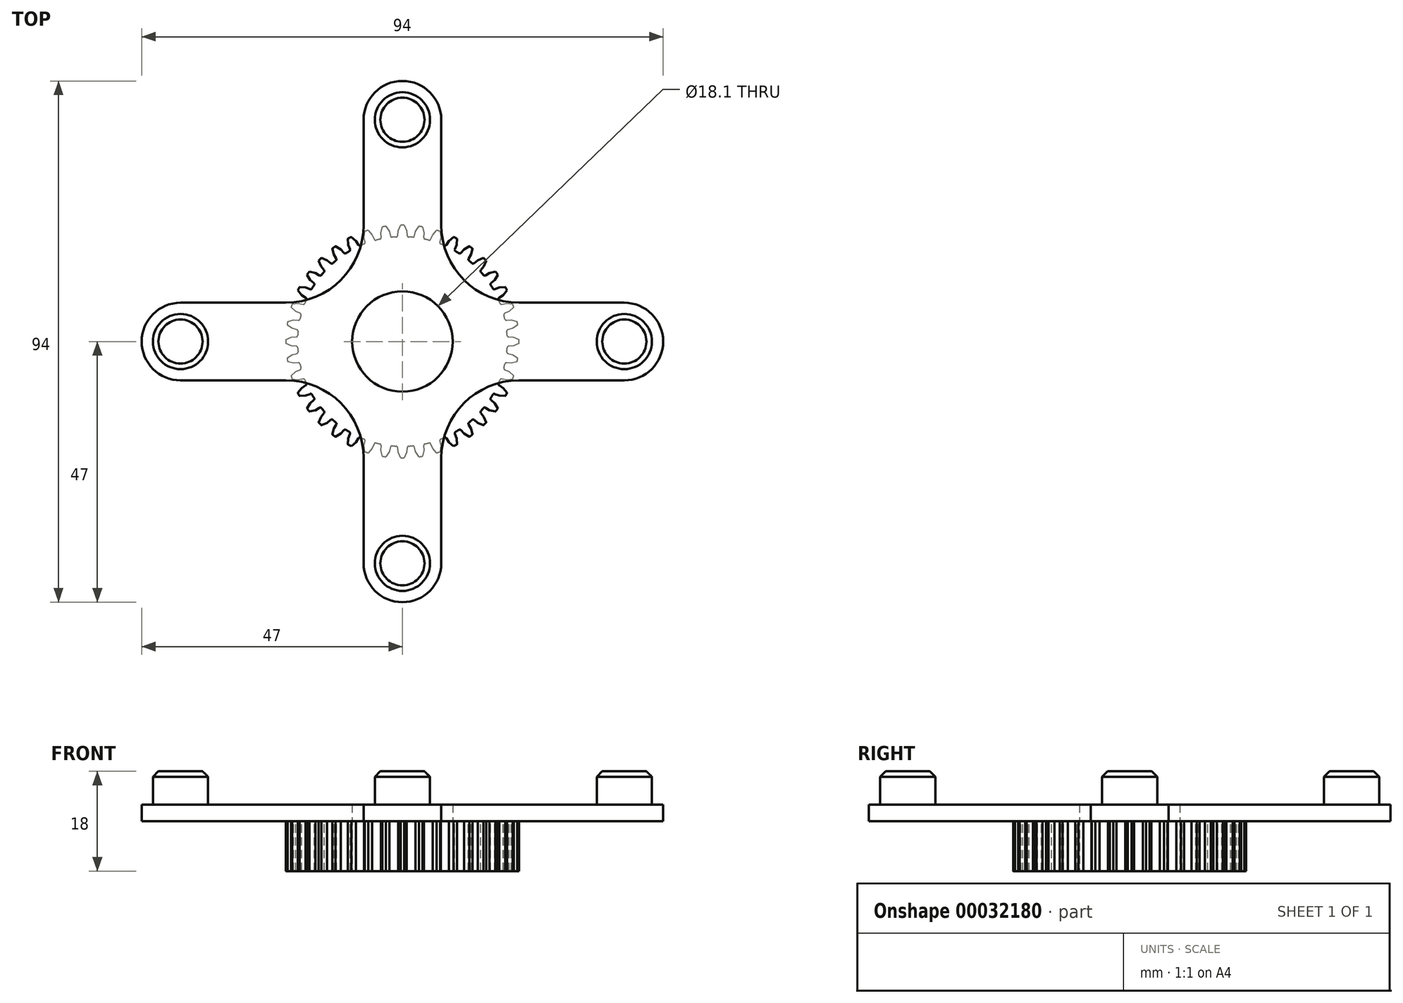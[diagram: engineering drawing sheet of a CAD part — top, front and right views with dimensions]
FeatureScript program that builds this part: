
annotation { "Feature Type Name" : "Feature", "Feature Type Description" : "" }
export const myFeature = defineFeature(function(context is Context, id is Id, definition is map)
    precondition{}
    {
        {
            var Q0;
            Q0=qCreatedBy(makeId("Top.planeOp"),FACE);
            var sketch = newSketch(context, id + "F0", { "sketchPlane" : qUnion([Q0])});
            skCircle(sketch, "E0", {"center": v(0, 0) * mm, "radius": 1 * mm});
            skCircle(sketch, "E1", {"center": v(0, 0) * mm, "radius": 52.75 * mm});
            skCircle(sketch, "E2", {"center": v(0, 40) * mm, "radius": 1 * mm});
            skCircle(sketch, "E3", {"center": v(40, 0) * mm, "radius": 1 * mm});
            skCircle(sketch, "E4", {"center": v(0, -40) * mm, "radius": 1 * mm});
            skCircle(sketch, "E5", {"center": v(-40, 0) * mm, "radius": 1 * mm});
            skCircle(sketch, "E6", {"center": v(0, 40) * mm, "radius": 4.97 * mm});
            skCircle(sketch, "E7", {"center": v(-40, 0) * mm, "radius": 4.97 * mm});
            skCircle(sketch, "E8", {"center": v(40, 0) * mm, "radius": 4.97 * mm});
            skCircle(sketch, "E9", {"center": v(0, -40) * mm, "radius": 4.97 * mm});
            skCircle(sketch, "E10", {"center": v(0, 0) * mm, "radius": 40 * mm, "construction": true});
            skArc(sketch, "E11.0.startCap", {"start": v(-7, 40) * mm, "mid": v(0, 47) * mm, "end": v(7, 40) * mm});
            skArc(sketch, "E11.0.endCap", {"start": v(7, -40) * mm, "mid": v(0, -47) * mm, "end": v(-7, -40) * mm});
            skLineSegment(sketch, "E11.0.left", {"start": v(7, 40) * mm, "end": v(7, 21) * mm});
            skLineSegment(sketch, "E11.0.right", {"start": v(-7, 40) * mm, "end": v(-7, 21) * mm});
            skArc(sketch, "E12.0.startCap", {"start": v(40, 7) * mm, "mid": v(47, 0) * mm, "end": v(40, -7) * mm});
            skArc(sketch, "E12.0.endCap", {"start": v(-40, -7) * mm, "mid": v(-47, 0) * mm, "end": v(-40, 7) * mm});
            skLineSegment(sketch, "E12.0.left", {"start": v(40, -7) * mm, "end": v(21, -7) * mm});
            skLineSegment(sketch, "E12.0.right", {"start": v(40, 7) * mm, "end": v(21, 7) * mm});
            skLineSegment(sketch, "E13.trimOffspring", {"start": v(-21, 7) * mm, "end": v(-40, 7) * mm});
            skLineSegment(sketch, "E14.trimOffspring", {"start": v(-7, -21) * mm, "end": v(-7, -40) * mm});
            skLineSegment(sketch, "E15.trimOffspring", {"start": v(7, -21) * mm, "end": v(7, -40) * mm});
            skLineSegment(sketch, "E16.trimOffspring", {"start": v(-21, -7) * mm, "end": v(-40, -7) * mm});
            skPoint(sketch, "E17.visualSharp", {"position": v(-7, 7) * mm});
            skArc(sketch, "E17.filletArc", {"start": v(-21, 7) * mm, "mid": v(-11.1, 11.1) * mm, "end": v(-7, 21) * mm});
            skPoint(sketch, "E18.visualSharp", {"position": v(-7, -7) * mm});
            skArc(sketch, "E18.filletArc", {"start": v(-7, -21) * mm, "mid": v(-11.1, -11.1) * mm, "end": v(-21, -7) * mm});
            skPoint(sketch, "E19.visualSharp", {"position": v(7, -7) * mm});
            skArc(sketch, "E19.filletArc", {"start": v(21, -7) * mm, "mid": v(11.1, -11.1) * mm, "end": v(7, -21) * mm});
            skPoint(sketch, "E20.visualSharp", {"position": v(7, 7) * mm});
            skArc(sketch, "E20.filletArc", {"start": v(7, 21) * mm, "mid": v(11.1, 11.1) * mm, "end": v(21, 7) * mm});
            skCircle(sketch, "E21", {"center": v(0, 0) * mm, "radius": 5 * mm});
            skCircle(sketch, "E22", {"center": v(0, 0) * mm, "radius": 14 * mm});
            skCircle(sketch, "E23", {"center": v(0, 0) * mm, "radius": 47 * mm, "construction": true});
            skSolve(sketch);
        }
        {
            var Q0;
            Q0=makeQuery(id+"F0.imprint","IMPRINT",FACE,{"disambiguationData":[TD([[makeQuery(id+"F0.imprint","IMPRINT",EDGE,{"derivedFrom":sQuery(id+"F0.wireOp",EDGE,"E6")}),-1.0]])]});
            var Q1;
            Q1=makeQuery(id+"F0.imprint","IMPRINT",FACE,{"disambiguationData":[TD([[makeQuery(id+"F0.imprint","IMPRINT",EDGE,{"derivedFrom":sQuery(id+"F0.wireOp",EDGE,"E5")}),1.0]])]});
            var Q2;
            Q2=makeQuery(id+"F0.imprint","IMPRINT",FACE,{"disambiguationData":[TD([[makeQuery(id+"F0.imprint","IMPRINT",EDGE,{"derivedFrom":sQuery(id+"F0.wireOp",EDGE,"E21")}),-1.0]])]});
            var Q3;
            Q3=makeQuery(id+"F0.imprint","IMPRINT",FACE,{"disambiguationData":[TD([[makeQuery(id+"F0.imprint","IMPRINT",EDGE,{"derivedFrom":sQuery(id+"F0.wireOp",EDGE,"E3")}),1.0]])]});
            var Q4;
            Q4=makeQuery(id+"F0.imprint","IMPRINT",FACE,{"disambiguationData":[TD([[makeQuery(id+"F0.imprint","IMPRINT",EDGE,{"derivedFrom":sQuery(id+"F0.wireOp",EDGE,"E2")}),1.0]])]});
            var Q5;
            Q5=makeQuery(id+"F0.imprint","IMPRINT",FACE,{"disambiguationData":[TD([[makeQuery(id+"F0.imprint","IMPRINT",EDGE,{"derivedFrom":sQuery(id+"F0.wireOp",EDGE,"E4")}),1.0]])]});
            var Q6;
            Q6=makeQuery(id+"F0.imprint","IMPRINT",FACE,{"disambiguationData":[TD([[makeQuery(id+"F0.imprint","IMPRINT",EDGE,{"derivedFrom":sQuery(id+"F0.wireOp",EDGE,"E5")}),-1.0]])]});
            var Q7;
            Q7=makeQuery(id+"F0.imprint","IMPRINT",FACE,{"disambiguationData":[TD([[makeQuery(id+"F0.imprint","IMPRINT",EDGE,{"derivedFrom":sQuery(id+"F0.wireOp",EDGE,"E4")}),-1.0]])]});
            var Q8;
            Q8=makeQuery(id+"F0.imprint","IMPRINT",FACE,{"disambiguationData":[TD([[makeQuery(id+"F0.imprint","IMPRINT",EDGE,{"derivedFrom":sQuery(id+"F0.wireOp",EDGE,"E3")}),-1.0]])]});
            var Q9;
            Q9=makeQuery(id+"F0.imprint","IMPRINT",FACE,{"disambiguationData":[TD([[makeQuery(id+"F0.imprint","IMPRINT",EDGE,{"derivedFrom":sQuery(id+"F0.wireOp",EDGE,"E2")}),-1.0]])]});
            extrude(context, id + "F1", {"entities" : qUnion([Q0, Q1, Q2, Q3, Q4, Q5, Q6, Q7, Q8, Q9]), "depth" : 3 * mm});
        }
        {
            var Q0;
            Q0=makeQuery(id+"F0.imprint","IMPRINT",FACE,{"disambiguationData":[TD([[makeQuery(id+"F0.imprint","IMPRINT",EDGE,{"derivedFrom":sQuery(id+"F0.wireOp",EDGE,"E5")}),1.0]])]});
            var Q1;
            Q1=makeQuery(id+"F0.imprint","IMPRINT",FACE,{"disambiguationData":[TD([[makeQuery(id+"F0.imprint","IMPRINT",EDGE,{"derivedFrom":sQuery(id+"F0.wireOp",EDGE,"E5")}),-1.0]])]});
            var Q2;
            Q2=makeQuery(id+"F0.imprint","IMPRINT",FACE,{"disambiguationData":[TD([[makeQuery(id+"F0.imprint","IMPRINT",EDGE,{"derivedFrom":sQuery(id+"F0.wireOp",EDGE,"E4")}),1.0]])]});
            var Q3;
            Q3=makeQuery(id+"F0.imprint","IMPRINT",FACE,{"disambiguationData":[TD([[makeQuery(id+"F0.imprint","IMPRINT",EDGE,{"derivedFrom":sQuery(id+"F0.wireOp",EDGE,"E4")}),-1.0]])]});
            var Q4;
            Q4=makeQuery(id+"F0.imprint","IMPRINT",FACE,{"disambiguationData":[TD([[makeQuery(id+"F0.imprint","IMPRINT",EDGE,{"derivedFrom":sQuery(id+"F0.wireOp",EDGE,"E3")}),-1.0]])]});
            var Q5;
            Q5=makeQuery(id+"F0.imprint","IMPRINT",FACE,{"disambiguationData":[TD([[makeQuery(id+"F0.imprint","IMPRINT",EDGE,{"derivedFrom":sQuery(id+"F0.wireOp",EDGE,"E3")}),1.0]])]});
            var Q6;
            Q6=makeQuery(id+"F0.imprint","IMPRINT",FACE,{"disambiguationData":[TD([[makeQuery(id+"F0.imprint","IMPRINT",EDGE,{"derivedFrom":sQuery(id+"F0.wireOp",EDGE,"E2")}),1.0]])]});
            var Q7;
            Q7=makeQuery(id+"F0.imprint","IMPRINT",FACE,{"disambiguationData":[TD([[makeQuery(id+"F0.imprint","IMPRINT",EDGE,{"derivedFrom":sQuery(id+"F0.wireOp",EDGE,"E2")}),-1.0]])]});
            extrude(context, id + "F2", {"entities" : qUnion([Q0, Q1, Q2, Q3, Q4, Q5, Q6, Q7]), "operationType" : NewBodyOperationType.ADD, "depth" : 9 * mm});
        }
        {
            var Q0;
            Q0=makeQuery(id+"F2.opExtrude","CAP_EDGE",EDGE,{"disambiguationData":[OSD([sQuery(id+"F0.wireOp",EDGE,"E7")])],"isStart":false});
            var Q1;
            Q1=makeQuery(id+"F2.opExtrude","CAP_EDGE",EDGE,{"disambiguationData":[OSD([sQuery(id+"F0.wireOp",EDGE,"E6")])],"isStart":false});
            var Q2;
            Q2=makeQuery(id+"F2.opExtrude","CAP_EDGE",EDGE,{"disambiguationData":[OSD([sQuery(id+"F0.wireOp",EDGE,"E8")])],"isStart":false});
            var Q3;
            Q3=makeQuery(id+"F2.opExtrude","CAP_EDGE",EDGE,{"disambiguationData":[OSD([sQuery(id+"F0.wireOp",EDGE,"E9")])],"isStart":false});
            var Q4;
            Q4=makeQuery(id+"FGKay2Df9lcGa7H_1.opExtrude","CAP_EDGE",EDGE,{"disambiguationData":[OSD([sQuery(id+"F0.wireOp",EDGE,"E21")])],"isStart":false});
            var Q5;
            Q5=makeQuery(id+"FGKay2Df9lcGa7H_1.opExtrude","CAP_EDGE",EDGE,{"disambiguationData":[OSD([sQuery(id+"F0.wireOp",EDGE,"E22")])],"isStart":false});
            chamfer(context, id + "F3", {"entities" : qUnion([Q0, Q1, Q2, Q3, Q4, Q5]), "width" : 1 * mm, "tangentPropagation" : true});
        }
        {
            var Q0;
            Q0=makeQuery(id+"F1.opExtrude","CAP_FACE",FACE,{"disambiguationData":[OSD([sQuery(id+"F0.wireOp",EDGE,"E11.0.startCap"),sQuery(id+"F0.wireOp",EDGE,"E11.0.endCap"),sQuery(id+"F0.wireOp",EDGE,"E11.0.left"),sQuery(id+"F0.wireOp",EDGE,"E11.0.right"),sQuery(id+"F0.wireOp",EDGE,"E12.0.startCap"),sQuery(id+"F0.wireOp",EDGE,"E12.0.endCap"),sQuery(id+"F0.wireOp",EDGE,"E12.0.left"),sQuery(id+"F0.wireOp",EDGE,"E12.0.right"),sQuery(id+"F0.wireOp",EDGE,"E13.trimOffspring"),sQuery(id+"F0.wireOp",EDGE,"E14.trimOffspring"),sQuery(id+"F0.wireOp",EDGE,"E15.trimOffspring"),sQuery(id+"F0.wireOp",EDGE,"E16.trimOffspring"),sQuery(id+"F0.wireOp",EDGE,"E17.filletArc"),sQuery(id+"F0.wireOp",EDGE,"E18.filletArc"),sQuery(id+"F0.wireOp",EDGE,"E19.filletArc"),sQuery(id+"F0.wireOp",EDGE,"E20.filletArc"),sQuery(id+"F0.wireOp",EDGE,"E21")])],"isStart":true});
            var sketch = newSketch(context, id + "F4", { "sketchPlane" : qUnion([Q0])});
            skArc(sketch, "E24", {"start": v(21, -0.33) * mm, "mid": v(21, -0.17) * mm, "end": v(21, 0) * mm});
            skArc(sketch, "E25", {"start": v(-12.5, 0) * mm, "mid": v(0, -12.5) * mm, "end": v(12.5, 0) * mm});
            skArc(sketch, "E26", {"start": v(0, -5) * mm, "mid": v(5, 0) * mm, "end": v(0, 5) * mm});
            skArc(sketch, "E27", {"start": v(-21, 0) * mm, "mid": v(-21, -0.17) * mm, "end": v(-21, -0.33) * mm});
            skArc(sketch, "E28", {"start": v(18.87, 1.14) * mm, "mid": v(18.84, 1.48) * mm, "end": v(18.81, 1.83) * mm});
            skArc(sketch, "E29", {"start": v(19.04, 2.15) * mm, "mid": v(18.86, 2.03) * mm, "end": v(18.81, 1.83) * mm});
            skLineSegment(sketch, "E30", {"start": v(19.04, 2.15) * mm, "end": v(19.86, 2.36) * mm});
            skArc(sketch, "E31", {"start": v(19.14, -0.86) * mm, "mid": v(18.95, -0.95) * mm, "end": v(18.87, -1.14) * mm});
            skLineSegment(sketch, "E32", {"start": v(19.86, 2.36) * mm, "end": v(20.8, 2.96) * mm});
            skArc(sketch, "E33", {"start": v(18.46, 4.07) * mm, "mid": v(18.38, 4.41) * mm, "end": v(18.3, 4.75) * mm});
            skLineSegment(sketch, "E34", {"start": v(19.14, -0.86) * mm, "end": v(19.98, -0.78) * mm});
            skArc(sketch, "E35", {"start": v(18.46, 5.1) * mm, "mid": v(18.31, 4.96) * mm, "end": v(18.3, 4.75) * mm});
            skLineSegment(sketch, "E36", {"start": v(19.98, -0.78) * mm, "end": v(21, -0.33) * mm});
            skLineSegment(sketch, "E37", {"start": v(18.46, 5.1) * mm, "end": v(19.25, 5.44) * mm});
            skArc(sketch, "E38", {"start": v(18.77, -3.84) * mm, "mid": v(18.57, -3.9) * mm, "end": v(18.46, -4.07) * mm});
            skLineSegment(sketch, "E39", {"start": v(19.25, 5.44) * mm, "end": v(20.07, 6.17) * mm});
            skArc(sketch, "E40", {"start": v(17.6, 6.91) * mm, "mid": v(17.46, 7.23) * mm, "end": v(17.33, 7.55) * mm});
            skLineSegment(sketch, "E41", {"start": v(18.77, -3.84) * mm, "end": v(19.62, -3.9) * mm});
            skArc(sketch, "E42", {"start": v(17.44, 7.93) * mm, "mid": v(17.31, 7.76) * mm, "end": v(17.33, 7.55) * mm});
            skLineSegment(sketch, "E43", {"start": v(19.62, -3.9) * mm, "end": v(20.69, -3.61) * mm});
            skLineSegment(sketch, "E44", {"start": v(17.44, 7.93) * mm, "end": v(18.16, 8.38) * mm});
            skArc(sketch, "E45", {"start": v(17.94, -6.73) * mm, "mid": v(17.73, -6.76) * mm, "end": v(17.6, -6.91) * mm});
            skLineSegment(sketch, "E46", {"start": v(18.16, 8.38) * mm, "end": v(18.86, 9.24) * mm});
            skArc(sketch, "E47", {"start": v(16.3, 9.58) * mm, "mid": v(16.11, 9.88) * mm, "end": v(15.93, 10.17) * mm});
            skLineSegment(sketch, "E48", {"start": v(17.94, -6.73) * mm, "end": v(18.77, -6.91) * mm});
            skArc(sketch, "E49", {"start": v(15.98, 10.56) * mm, "mid": v(15.89, 10.37) * mm, "end": v(15.93, 10.17) * mm});
            skLineSegment(sketch, "E50", {"start": v(18.77, -6.91) * mm, "end": v(19.87, -6.8) * mm});
            skLineSegment(sketch, "E51", {"start": v(15.98, 10.56) * mm, "end": v(16.62, 11.12) * mm});
            skArc(sketch, "E52", {"start": v(16.66, -9.45) * mm, "mid": v(16.45, -9.45) * mm, "end": v(16.3, -9.58) * mm});
            skLineSegment(sketch, "E53", {"start": v(16.62, 11.12) * mm, "end": v(17.18, 12.07) * mm});
            skArc(sketch, "E54", {"start": v(14.6, 12) * mm, "mid": v(14.37, 12.27) * mm, "end": v(14.14, 12.54) * mm});
            skLineSegment(sketch, "E55", {"start": v(16.66, -9.45) * mm, "end": v(17.45, -9.76) * mm});
            skArc(sketch, "E56", {"start": v(14.14, 12.93) * mm, "mid": v(14.07, 12.73) * mm, "end": v(14.14, 12.54) * mm});
            skLineSegment(sketch, "E57", {"start": v(17.45, -9.76) * mm, "end": v(18.56, -9.83) * mm});
            skLineSegment(sketch, "E58", {"start": v(14.14, 12.93) * mm, "end": v(14.68, 13.58) * mm});
            skArc(sketch, "E59", {"start": v(14.98, -11.94) * mm, "mid": v(14.77, -11.9) * mm, "end": v(14.6, -12) * mm});
            skLineSegment(sketch, "E60", {"start": v(14.68, 13.58) * mm, "end": v(15.08, 14.61) * mm});
            skArc(sketch, "E61", {"start": v(12.54, 14.14) * mm, "mid": v(12.27, 14.37) * mm, "end": v(12, 14.6) * mm});
            skLineSegment(sketch, "E62", {"start": v(14.98, -11.94) * mm, "end": v(15.71, -12.37) * mm});
            skArc(sketch, "E63", {"start": v(11.94, 14.98) * mm, "mid": v(11.9, 14.77) * mm, "end": v(12, 14.6) * mm});
            skLineSegment(sketch, "E64", {"start": v(15.71, -12.37) * mm, "end": v(16.8, -12.61) * mm});
            skArc(sketch, "E65", {"start": v(12.93, -14.14) * mm, "mid": v(12.73, -14.07) * mm, "end": v(12.54, -14.14) * mm});
            skLineSegment(sketch, "E66", {"start": v(11.94, 14.98) * mm, "end": v(12.37, 15.71) * mm});
            skLineSegment(sketch, "E67", {"start": v(12.93, -14.14) * mm, "end": v(13.58, -14.68) * mm});
            skLineSegment(sketch, "E68", {"start": v(12.37, 15.71) * mm, "end": v(12.61, 16.8) * mm});
            skArc(sketch, "E69", {"start": v(10.17, 15.93) * mm, "mid": v(9.88, 16.11) * mm, "end": v(9.58, 16.3) * mm});
            skLineSegment(sketch, "E70", {"start": v(13.58, -14.68) * mm, "end": v(14.61, -15.08) * mm});
            skArc(sketch, "E71", {"start": v(9.45, 16.66) * mm, "mid": v(9.45, 16.45) * mm, "end": v(9.58, 16.3) * mm});
            skArc(sketch, "E72", {"start": v(10.56, -15.98) * mm, "mid": v(10.37, -15.89) * mm, "end": v(10.17, -15.93) * mm});
            skLineSegment(sketch, "E73", {"start": v(9.45, 16.66) * mm, "end": v(9.76, 17.45) * mm});
            skLineSegment(sketch, "E74", {"start": v(10.56, -15.98) * mm, "end": v(11.12, -16.62) * mm});
            skLineSegment(sketch, "E75", {"start": v(9.76, 17.45) * mm, "end": v(9.83, 18.56) * mm});
            skArc(sketch, "E76", {"start": v(7.55, 17.33) * mm, "mid": v(7.23, 17.46) * mm, "end": v(6.91, 17.6) * mm});
            skLineSegment(sketch, "E77", {"start": v(11.12, -16.62) * mm, "end": v(12.07, -17.18) * mm});
            skArc(sketch, "E78", {"start": v(6.73, 17.94) * mm, "mid": v(6.76, 17.73) * mm, "end": v(6.91, 17.6) * mm});
            skArc(sketch, "E79", {"start": v(7.93, -17.44) * mm, "mid": v(7.76, -17.31) * mm, "end": v(7.55, -17.33) * mm});
            skLineSegment(sketch, "E80", {"start": v(6.73, 17.94) * mm, "end": v(6.91, 18.77) * mm});
            skLineSegment(sketch, "E81", {"start": v(7.93, -17.44) * mm, "end": v(8.38, -18.16) * mm});
            skLineSegment(sketch, "E82", {"start": v(6.91, 18.77) * mm, "end": v(6.8, 19.87) * mm});
            skArc(sketch, "E83", {"start": v(4.75, 18.3) * mm, "mid": v(4.41, 18.38) * mm, "end": v(4.07, 18.46) * mm});
            skLineSegment(sketch, "E84", {"start": v(8.38, -18.16) * mm, "end": v(9.24, -18.86) * mm});
            skArc(sketch, "E85", {"start": v(3.84, 18.77) * mm, "mid": v(3.9, 18.57) * mm, "end": v(4.07, 18.46) * mm});
            skArc(sketch, "E86", {"start": v(5.1, -18.46) * mm, "mid": v(4.96, -18.31) * mm, "end": v(4.75, -18.3) * mm});
            skLineSegment(sketch, "E87", {"start": v(3.84, 18.77) * mm, "end": v(3.9, 19.62) * mm});
            skLineSegment(sketch, "E88", {"start": v(5.1, -18.46) * mm, "end": v(5.44, -19.25) * mm});
            skLineSegment(sketch, "E89", {"start": v(3.9, 19.62) * mm, "end": v(3.61, 20.69) * mm});
            skArc(sketch, "E90", {"start": v(1.83, 18.81) * mm, "mid": v(1.48, 18.84) * mm, "end": v(1.14, 18.87) * mm});
            skLineSegment(sketch, "E91", {"start": v(5.44, -19.25) * mm, "end": v(6.17, -20.07) * mm});
            skArc(sketch, "E92", {"start": v(0.86, 19.14) * mm, "mid": v(0.95, 18.95) * mm, "end": v(1.14, 18.87) * mm});
            skArc(sketch, "E93", {"start": v(2.15, -19.04) * mm, "mid": v(2.03, -18.86) * mm, "end": v(1.83, -18.81) * mm});
            skLineSegment(sketch, "E94", {"start": v(0.86, 19.14) * mm, "end": v(0.78, 19.98) * mm});
            skArc(sketch, "E95", {"start": v(-1.14, 18.87) * mm, "mid": v(-1.48, 18.84) * mm, "end": v(-1.83, 18.81) * mm});
            skLineSegment(sketch, "E96", {"start": v(2.15, -19.04) * mm, "end": v(2.36, -19.86) * mm});
            skLineSegment(sketch, "E97", {"start": v(0.78, 19.98) * mm, "end": v(0.33, 21) * mm});
            skArc(sketch, "E98", {"start": v(-2.15, 19.04) * mm, "mid": v(-2.03, 18.86) * mm, "end": v(-1.83, 18.81) * mm});
            skLineSegment(sketch, "E99", {"start": v(2.36, -19.86) * mm, "end": v(2.96, -20.8) * mm});
            skArc(sketch, "E100", {"start": v(-0.86, -19.14) * mm, "mid": v(-0.95, -18.95) * mm, "end": v(-1.14, -18.87) * mm});
            skLineSegment(sketch, "E101", {"start": v(-2.15, 19.04) * mm, "end": v(-2.36, 19.86) * mm});
            skLineSegment(sketch, "E102", {"start": v(-0.86, -19.14) * mm, "end": v(-0.78, -19.98) * mm});
            skLineSegment(sketch, "E103", {"start": v(-2.36, 19.86) * mm, "end": v(-2.96, 20.8) * mm});
            skArc(sketch, "E104", {"start": v(-4.07, 18.46) * mm, "mid": v(-4.41, 18.38) * mm, "end": v(-4.75, 18.3) * mm});
            skLineSegment(sketch, "E105", {"start": v(-0.78, -19.98) * mm, "end": v(-0.33, -21) * mm});
            skArc(sketch, "E106", {"start": v(-5.1, 18.46) * mm, "mid": v(-4.96, 18.31) * mm, "end": v(-4.75, 18.3) * mm});
            skArc(sketch, "E107", {"start": v(-3.84, -18.77) * mm, "mid": v(-3.9, -18.57) * mm, "end": v(-4.07, -18.46) * mm});
            skLineSegment(sketch, "E108", {"start": v(-5.1, 18.46) * mm, "end": v(-5.44, 19.25) * mm});
            skLineSegment(sketch, "E109", {"start": v(-3.84, -18.77) * mm, "end": v(-3.9, -19.62) * mm});
            skLineSegment(sketch, "E110", {"start": v(-5.44, 19.25) * mm, "end": v(-6.17, 20.07) * mm});
            skArc(sketch, "E111", {"start": v(-6.91, 17.6) * mm, "mid": v(-7.23, 17.46) * mm, "end": v(-7.55, 17.33) * mm});
            skLineSegment(sketch, "E112", {"start": v(-3.9, -19.62) * mm, "end": v(-3.61, -20.69) * mm});
            skArc(sketch, "E113", {"start": v(-7.93, 17.44) * mm, "mid": v(-7.76, 17.31) * mm, "end": v(-7.55, 17.33) * mm});
            skArc(sketch, "E114", {"start": v(-6.73, -17.94) * mm, "mid": v(-6.76, -17.73) * mm, "end": v(-6.91, -17.6) * mm});
            skLineSegment(sketch, "E115", {"start": v(-7.93, 17.44) * mm, "end": v(-8.38, 18.16) * mm});
            skLineSegment(sketch, "E116", {"start": v(-6.73, -17.94) * mm, "end": v(-6.91, -18.77) * mm});
            skLineSegment(sketch, "E117", {"start": v(-8.38, 18.16) * mm, "end": v(-9.24, 18.86) * mm});
            skArc(sketch, "E118", {"start": v(-9.58, 16.3) * mm, "mid": v(-9.88, 16.11) * mm, "end": v(-10.17, 15.93) * mm});
            skLineSegment(sketch, "E119", {"start": v(-6.91, -18.77) * mm, "end": v(-6.8, -19.87) * mm});
            skArc(sketch, "E120", {"start": v(-10.56, 15.98) * mm, "mid": v(-10.37, 15.89) * mm, "end": v(-10.17, 15.93) * mm});
            skArc(sketch, "E121", {"start": v(-9.45, -16.66) * mm, "mid": v(-9.45, -16.45) * mm, "end": v(-9.58, -16.3) * mm});
            skLineSegment(sketch, "E122", {"start": v(-10.56, 15.98) * mm, "end": v(-11.12, 16.62) * mm});
            skLineSegment(sketch, "E123", {"start": v(-9.45, -16.66) * mm, "end": v(-9.76, -17.45) * mm});
            skLineSegment(sketch, "E124", {"start": v(-11.12, 16.62) * mm, "end": v(-12.07, 17.18) * mm});
            skArc(sketch, "E125", {"start": v(-12, 14.6) * mm, "mid": v(-12.27, 14.37) * mm, "end": v(-12.54, 14.14) * mm});
            skLineSegment(sketch, "E126", {"start": v(-9.76, -17.45) * mm, "end": v(-9.83, -18.56) * mm});
            skArc(sketch, "E127", {"start": v(-12.93, 14.14) * mm, "mid": v(-12.73, 14.07) * mm, "end": v(-12.54, 14.14) * mm});
            skArc(sketch, "E128", {"start": v(-11.94, -14.98) * mm, "mid": v(-11.9, -14.77) * mm, "end": v(-12, -14.6) * mm});
            skLineSegment(sketch, "E129", {"start": v(-12.93, 14.14) * mm, "end": v(-13.58, 14.68) * mm});
            skLineSegment(sketch, "E130", {"start": v(-11.94, -14.98) * mm, "end": v(-12.37, -15.71) * mm});
            skLineSegment(sketch, "E131", {"start": v(-13.58, 14.68) * mm, "end": v(-14.61, 15.08) * mm});
            skArc(sketch, "E132", {"start": v(-14.14, 12.54) * mm, "mid": v(-14.37, 12.27) * mm, "end": v(-14.6, 12) * mm});
            skLineSegment(sketch, "E133", {"start": v(-12.37, -15.71) * mm, "end": v(-12.61, -16.8) * mm});
            skArc(sketch, "E134", {"start": v(-14.98, 11.94) * mm, "mid": v(-14.77, 11.9) * mm, "end": v(-14.6, 12) * mm});
            skArc(sketch, "E135", {"start": v(-14.14, -12.93) * mm, "mid": v(-14.07, -12.73) * mm, "end": v(-14.14, -12.54) * mm});
            skLineSegment(sketch, "E136", {"start": v(-14.98, 11.94) * mm, "end": v(-15.71, 12.37) * mm});
            skLineSegment(sketch, "E137", {"start": v(-14.14, -12.93) * mm, "end": v(-14.68, -13.58) * mm});
            skLineSegment(sketch, "E138", {"start": v(-15.71, 12.37) * mm, "end": v(-16.8, 12.61) * mm});
            skArc(sketch, "E139", {"start": v(-15.93, 10.17) * mm, "mid": v(-16.11, 9.88) * mm, "end": v(-16.3, 9.58) * mm});
            skLineSegment(sketch, "E140", {"start": v(-14.68, -13.58) * mm, "end": v(-15.08, -14.61) * mm});
            skArc(sketch, "E141", {"start": v(-16.66, 9.45) * mm, "mid": v(-16.45, 9.45) * mm, "end": v(-16.3, 9.58) * mm});
            skArc(sketch, "E142", {"start": v(-15.98, -10.56) * mm, "mid": v(-15.89, -10.37) * mm, "end": v(-15.93, -10.17) * mm});
            skLineSegment(sketch, "E143", {"start": v(-16.66, 9.45) * mm, "end": v(-17.45, 9.76) * mm});
            skLineSegment(sketch, "E144", {"start": v(-15.98, -10.56) * mm, "end": v(-16.62, -11.12) * mm});
            skLineSegment(sketch, "E145", {"start": v(-17.45, 9.76) * mm, "end": v(-18.56, 9.83) * mm});
            skArc(sketch, "E146", {"start": v(-17.33, 7.55) * mm, "mid": v(-17.46, 7.23) * mm, "end": v(-17.6, 6.91) * mm});
            skLineSegment(sketch, "E147", {"start": v(-16.62, -11.12) * mm, "end": v(-17.18, -12.07) * mm});
            skArc(sketch, "E148", {"start": v(-17.94, 6.73) * mm, "mid": v(-17.73, 6.76) * mm, "end": v(-17.6, 6.91) * mm});
            skArc(sketch, "E149", {"start": v(-17.44, -7.93) * mm, "mid": v(-17.31, -7.76) * mm, "end": v(-17.33, -7.55) * mm});
            skLineSegment(sketch, "E150", {"start": v(-17.94, 6.73) * mm, "end": v(-18.77, 6.91) * mm});
            skLineSegment(sketch, "E151", {"start": v(-17.44, -7.93) * mm, "end": v(-18.16, -8.38) * mm});
            skLineSegment(sketch, "E152", {"start": v(-18.77, 6.91) * mm, "end": v(-19.87, 6.8) * mm});
            skArc(sketch, "E153", {"start": v(-18.3, 4.75) * mm, "mid": v(-18.38, 4.41) * mm, "end": v(-18.46, 4.07) * mm});
            skLineSegment(sketch, "E154", {"start": v(-18.16, -8.38) * mm, "end": v(-18.86, -9.24) * mm});
            skArc(sketch, "E155", {"start": v(-18.77, 3.84) * mm, "mid": v(-18.57, 3.9) * mm, "end": v(-18.46, 4.07) * mm});
            skArc(sketch, "E156", {"start": v(-18.46, -5.1) * mm, "mid": v(-18.31, -4.96) * mm, "end": v(-18.3, -4.75) * mm});
            skLineSegment(sketch, "E157", {"start": v(-18.77, 3.84) * mm, "end": v(-19.62, 3.9) * mm});
            skLineSegment(sketch, "E158", {"start": v(-18.46, -5.1) * mm, "end": v(-19.25, -5.44) * mm});
            skLineSegment(sketch, "E159", {"start": v(-19.62, 3.9) * mm, "end": v(-20.69, 3.61) * mm});
            skArc(sketch, "E160", {"start": v(-18.81, 1.83) * mm, "mid": v(-18.84, 1.48) * mm, "end": v(-18.87, 1.14) * mm});
            skLineSegment(sketch, "E161", {"start": v(-19.25, -5.44) * mm, "end": v(-20.07, -6.17) * mm});
            skArc(sketch, "E162", {"start": v(-19.14, 0.86) * mm, "mid": v(-18.95, 0.95) * mm, "end": v(-18.87, 1.14) * mm});
            skLineSegment(sketch, "E163", {"start": v(-19.14, 0.86) * mm, "end": v(-19.98, 0.78) * mm});
            skArc(sketch, "E164", {"start": v(-19.04, -2.15) * mm, "mid": v(-18.86, -2.03) * mm, "end": v(-18.81, -1.83) * mm});
            skLineSegment(sketch, "E165", {"start": v(-19.04, -2.15) * mm, "end": v(-19.86, -2.36) * mm});
            skLineSegment(sketch, "E166", {"start": v(-19.98, 0.78) * mm, "end": v(-21, 0.33) * mm});
            skLineSegment(sketch, "E167", {"start": v(-19.86, -2.36) * mm, "end": v(-20.8, -2.96) * mm});
            skLineSegment(sketch, "E168", {"start": v(-21, -0.33) * mm, "end": v(-19.98, -0.78) * mm});
            skLineSegment(sketch, "E169", {"start": v(-19.98, -0.78) * mm, "end": v(-19.14, -0.86) * mm});
            skArc(sketch, "E170", {"start": v(-18.87, -1.14) * mm, "mid": v(-18.95, -0.95) * mm, "end": v(-19.14, -0.86) * mm});
            skArc(sketch, "E171", {"start": v(-18.87, -1.14) * mm, "mid": v(-18.84, -1.48) * mm, "end": v(-18.81, -1.83) * mm});
            skLineSegment(sketch, "E172", {"start": v(-20.69, -3.61) * mm, "end": v(-19.62, -3.9) * mm});
            skLineSegment(sketch, "E173", {"start": v(-19.62, -3.9) * mm, "end": v(-18.77, -3.84) * mm});
            skArc(sketch, "E174", {"start": v(-18.46, -4.07) * mm, "mid": v(-18.57, -3.9) * mm, "end": v(-18.77, -3.84) * mm});
            skArc(sketch, "E175", {"start": v(-18.46, -4.07) * mm, "mid": v(-18.38, -4.41) * mm, "end": v(-18.3, -4.75) * mm});
            skLineSegment(sketch, "E176", {"start": v(-19.87, -6.8) * mm, "end": v(-18.77, -6.91) * mm});
            skLineSegment(sketch, "E177", {"start": v(-18.77, -6.91) * mm, "end": v(-17.94, -6.73) * mm});
            skArc(sketch, "E178", {"start": v(-17.6, -6.91) * mm, "mid": v(-17.73, -6.76) * mm, "end": v(-17.94, -6.73) * mm});
            skArc(sketch, "E179", {"start": v(-17.6, -6.91) * mm, "mid": v(-17.46, -7.23) * mm, "end": v(-17.33, -7.55) * mm});
            skLineSegment(sketch, "E180", {"start": v(-18.56, -9.83) * mm, "end": v(-17.45, -9.76) * mm});
            skLineSegment(sketch, "E181", {"start": v(-17.45, -9.76) * mm, "end": v(-16.66, -9.45) * mm});
            skArc(sketch, "E182", {"start": v(-16.3, -9.58) * mm, "mid": v(-16.45, -9.45) * mm, "end": v(-16.66, -9.45) * mm});
            skArc(sketch, "E183", {"start": v(-16.3, -9.58) * mm, "mid": v(-16.11, -9.88) * mm, "end": v(-15.93, -10.17) * mm});
            skLineSegment(sketch, "E184", {"start": v(-16.8, -12.61) * mm, "end": v(-15.71, -12.37) * mm});
            skLineSegment(sketch, "E185", {"start": v(-15.71, -12.37) * mm, "end": v(-14.98, -11.94) * mm});
            skArc(sketch, "E186", {"start": v(-14.6, -12) * mm, "mid": v(-14.77, -11.9) * mm, "end": v(-14.98, -11.94) * mm});
            skArc(sketch, "E187", {"start": v(-14.6, -12) * mm, "mid": v(-14.37, -12.27) * mm, "end": v(-14.14, -12.54) * mm});
            skLineSegment(sketch, "E188", {"start": v(-14.61, -15.08) * mm, "end": v(-13.58, -14.68) * mm});
            skLineSegment(sketch, "E189", {"start": v(-13.58, -14.68) * mm, "end": v(-12.93, -14.14) * mm});
            skArc(sketch, "E190", {"start": v(-12.54, -14.14) * mm, "mid": v(-12.73, -14.07) * mm, "end": v(-12.93, -14.14) * mm});
            skArc(sketch, "E191", {"start": v(-12.54, -14.14) * mm, "mid": v(-12.27, -14.37) * mm, "end": v(-12, -14.6) * mm});
            skLineSegment(sketch, "E192", {"start": v(-12.07, -17.18) * mm, "end": v(-11.12, -16.62) * mm});
            skLineSegment(sketch, "E193", {"start": v(-11.12, -16.62) * mm, "end": v(-10.56, -15.98) * mm});
            skArc(sketch, "E194", {"start": v(-10.17, -15.93) * mm, "mid": v(-10.37, -15.89) * mm, "end": v(-10.56, -15.98) * mm});
            skArc(sketch, "E195", {"start": v(-10.17, -15.93) * mm, "mid": v(-9.88, -16.11) * mm, "end": v(-9.58, -16.3) * mm});
            skLineSegment(sketch, "E196", {"start": v(-9.24, -18.86) * mm, "end": v(-8.38, -18.16) * mm});
            skLineSegment(sketch, "E197", {"start": v(-8.38, -18.16) * mm, "end": v(-7.93, -17.44) * mm});
            skArc(sketch, "E198", {"start": v(-7.55, -17.33) * mm, "mid": v(-7.76, -17.31) * mm, "end": v(-7.93, -17.44) * mm});
            skArc(sketch, "E199", {"start": v(-7.55, -17.33) * mm, "mid": v(-7.23, -17.46) * mm, "end": v(-6.91, -17.6) * mm});
            skLineSegment(sketch, "E200", {"start": v(-6.17, -20.07) * mm, "end": v(-5.44, -19.25) * mm});
            skLineSegment(sketch, "E201", {"start": v(-5.44, -19.25) * mm, "end": v(-5.1, -18.46) * mm});
            skArc(sketch, "E202", {"start": v(-4.75, -18.3) * mm, "mid": v(-4.96, -18.31) * mm, "end": v(-5.1, -18.46) * mm});
            skArc(sketch, "E203", {"start": v(-4.75, -18.3) * mm, "mid": v(-4.41, -18.38) * mm, "end": v(-4.07, -18.46) * mm});
            skLineSegment(sketch, "E204", {"start": v(-2.96, -20.8) * mm, "end": v(-2.36, -19.86) * mm});
            skLineSegment(sketch, "E205", {"start": v(-2.36, -19.86) * mm, "end": v(-2.15, -19.04) * mm});
            skArc(sketch, "E206", {"start": v(-1.83, -18.81) * mm, "mid": v(-2.03, -18.86) * mm, "end": v(-2.15, -19.04) * mm});
            skArc(sketch, "E207", {"start": v(-1.83, -18.81) * mm, "mid": v(-1.48, -18.84) * mm, "end": v(-1.14, -18.87) * mm});
            skLineSegment(sketch, "E208", {"start": v(0.33, -21) * mm, "end": v(0.78, -19.98) * mm});
            skLineSegment(sketch, "E209", {"start": v(0.78, -19.98) * mm, "end": v(0.86, -19.14) * mm});
            skArc(sketch, "E210", {"start": v(1.14, -18.87) * mm, "mid": v(0.95, -18.95) * mm, "end": v(0.86, -19.14) * mm});
            skArc(sketch, "E211", {"start": v(1.14, -18.87) * mm, "mid": v(1.48, -18.84) * mm, "end": v(1.83, -18.81) * mm});
            skLineSegment(sketch, "E212", {"start": v(3.61, -20.69) * mm, "end": v(3.9, -19.62) * mm});
            skLineSegment(sketch, "E213", {"start": v(3.9, -19.62) * mm, "end": v(3.84, -18.77) * mm});
            skArc(sketch, "E214", {"start": v(4.07, -18.46) * mm, "mid": v(3.9, -18.57) * mm, "end": v(3.84, -18.77) * mm});
            skArc(sketch, "E215", {"start": v(4.07, -18.46) * mm, "mid": v(4.41, -18.38) * mm, "end": v(4.75, -18.3) * mm});
            skLineSegment(sketch, "E216", {"start": v(6.8, -19.87) * mm, "end": v(6.91, -18.77) * mm});
            skLineSegment(sketch, "E217", {"start": v(6.91, -18.77) * mm, "end": v(6.73, -17.94) * mm});
            skArc(sketch, "E218", {"start": v(6.91, -17.6) * mm, "mid": v(6.76, -17.73) * mm, "end": v(6.73, -17.94) * mm});
            skArc(sketch, "E219", {"start": v(6.91, -17.6) * mm, "mid": v(7.23, -17.46) * mm, "end": v(7.55, -17.33) * mm});
            skLineSegment(sketch, "E220", {"start": v(9.83, -18.56) * mm, "end": v(9.76, -17.45) * mm});
            skLineSegment(sketch, "E221", {"start": v(9.76, -17.45) * mm, "end": v(9.45, -16.66) * mm});
            skArc(sketch, "E222", {"start": v(9.58, -16.3) * mm, "mid": v(9.45, -16.45) * mm, "end": v(9.45, -16.66) * mm});
            skArc(sketch, "E223", {"start": v(9.58, -16.3) * mm, "mid": v(9.88, -16.11) * mm, "end": v(10.17, -15.93) * mm});
            skLineSegment(sketch, "E224", {"start": v(12.61, -16.8) * mm, "end": v(12.37, -15.71) * mm});
            skLineSegment(sketch, "E225", {"start": v(12.37, -15.71) * mm, "end": v(11.94, -14.98) * mm});
            skArc(sketch, "E226", {"start": v(12, -14.6) * mm, "mid": v(11.9, -14.77) * mm, "end": v(11.94, -14.98) * mm});
            skArc(sketch, "E227", {"start": v(12, -14.6) * mm, "mid": v(12.27, -14.37) * mm, "end": v(12.54, -14.14) * mm});
            skLineSegment(sketch, "E228", {"start": v(15.08, -14.61) * mm, "end": v(14.68, -13.58) * mm});
            skLineSegment(sketch, "E229", {"start": v(14.68, -13.58) * mm, "end": v(14.14, -12.93) * mm});
            skArc(sketch, "E230", {"start": v(14.14, -12.54) * mm, "mid": v(14.07, -12.73) * mm, "end": v(14.14, -12.93) * mm});
            skArc(sketch, "E231", {"start": v(14.14, -12.54) * mm, "mid": v(14.37, -12.27) * mm, "end": v(14.6, -12) * mm});
            skLineSegment(sketch, "E232", {"start": v(17.18, -12.07) * mm, "end": v(16.62, -11.12) * mm});
            skLineSegment(sketch, "E233", {"start": v(16.62, -11.12) * mm, "end": v(15.98, -10.56) * mm});
            skArc(sketch, "E234", {"start": v(15.93, -10.17) * mm, "mid": v(15.89, -10.37) * mm, "end": v(15.98, -10.56) * mm});
            skArc(sketch, "E235", {"start": v(15.93, -10.17) * mm, "mid": v(16.11, -9.88) * mm, "end": v(16.3, -9.58) * mm});
            skLineSegment(sketch, "E236", {"start": v(18.86, -9.24) * mm, "end": v(18.16, -8.38) * mm});
            skLineSegment(sketch, "E237", {"start": v(18.16, -8.38) * mm, "end": v(17.44, -7.93) * mm});
            skArc(sketch, "E238", {"start": v(17.33, -7.55) * mm, "mid": v(17.31, -7.76) * mm, "end": v(17.44, -7.93) * mm});
            skArc(sketch, "E239", {"start": v(17.33, -7.55) * mm, "mid": v(17.46, -7.23) * mm, "end": v(17.6, -6.91) * mm});
            skLineSegment(sketch, "E240", {"start": v(20.07, -6.17) * mm, "end": v(19.25, -5.44) * mm});
            skLineSegment(sketch, "E241", {"start": v(19.25, -5.44) * mm, "end": v(18.46, -5.1) * mm});
            skArc(sketch, "E242", {"start": v(18.3, -4.75) * mm, "mid": v(18.31, -4.96) * mm, "end": v(18.46, -5.1) * mm});
            skArc(sketch, "E243", {"start": v(18.3, -4.75) * mm, "mid": v(18.38, -4.41) * mm, "end": v(18.46, -4.07) * mm});
            skLineSegment(sketch, "E244", {"start": v(20.8, -2.96) * mm, "end": v(19.86, -2.36) * mm});
            skLineSegment(sketch, "E245", {"start": v(19.86, -2.36) * mm, "end": v(19.04, -2.15) * mm});
            skArc(sketch, "E246", {"start": v(18.81, -1.83) * mm, "mid": v(18.86, -2.03) * mm, "end": v(19.04, -2.15) * mm});
            skArc(sketch, "E247", {"start": v(18.81, -1.83) * mm, "mid": v(18.84, -1.48) * mm, "end": v(18.87, -1.14) * mm});
            skLineSegment(sketch, "E248", {"start": v(21, 0.33) * mm, "end": v(19.98, 0.78) * mm});
            skLineSegment(sketch, "E249", {"start": v(19.98, 0.78) * mm, "end": v(19.14, 0.86) * mm});
            skArc(sketch, "E250", {"start": v(18.87, 1.14) * mm, "mid": v(18.95, 0.95) * mm, "end": v(19.14, 0.86) * mm});
            skLineSegment(sketch, "E251", {"start": v(20.69, 3.61) * mm, "end": v(19.62, 3.9) * mm});
            skLineSegment(sketch, "E252", {"start": v(19.62, 3.9) * mm, "end": v(18.77, 3.84) * mm});
            skArc(sketch, "E253", {"start": v(18.46, 4.07) * mm, "mid": v(18.57, 3.9) * mm, "end": v(18.77, 3.84) * mm});
            skLineSegment(sketch, "E254", {"start": v(19.87, 6.8) * mm, "end": v(18.77, 6.91) * mm});
            skLineSegment(sketch, "E255", {"start": v(18.77, 6.91) * mm, "end": v(17.94, 6.73) * mm});
            skArc(sketch, "E256", {"start": v(17.6, 6.91) * mm, "mid": v(17.73, 6.76) * mm, "end": v(17.94, 6.73) * mm});
            skLineSegment(sketch, "E257", {"start": v(18.56, 9.83) * mm, "end": v(17.45, 9.76) * mm});
            skLineSegment(sketch, "E258", {"start": v(17.45, 9.76) * mm, "end": v(16.66, 9.45) * mm});
            skArc(sketch, "E259", {"start": v(16.3, 9.58) * mm, "mid": v(16.45, 9.45) * mm, "end": v(16.66, 9.45) * mm});
            skLineSegment(sketch, "E260", {"start": v(16.8, 12.61) * mm, "end": v(15.71, 12.37) * mm});
            skLineSegment(sketch, "E261", {"start": v(15.71, 12.37) * mm, "end": v(14.98, 11.94) * mm});
            skArc(sketch, "E262", {"start": v(14.6, 12) * mm, "mid": v(14.77, 11.9) * mm, "end": v(14.98, 11.94) * mm});
            skLineSegment(sketch, "E263", {"start": v(14.61, 15.08) * mm, "end": v(13.58, 14.68) * mm});
            skLineSegment(sketch, "E264", {"start": v(13.58, 14.68) * mm, "end": v(12.93, 14.14) * mm});
            skArc(sketch, "E265", {"start": v(12.54, 14.14) * mm, "mid": v(12.73, 14.07) * mm, "end": v(12.93, 14.14) * mm});
            skLineSegment(sketch, "E266", {"start": v(12.07, 17.18) * mm, "end": v(11.12, 16.62) * mm});
            skLineSegment(sketch, "E267", {"start": v(11.12, 16.62) * mm, "end": v(10.56, 15.98) * mm});
            skArc(sketch, "E268", {"start": v(10.17, 15.93) * mm, "mid": v(10.37, 15.89) * mm, "end": v(10.56, 15.98) * mm});
            skLineSegment(sketch, "E269", {"start": v(9.24, 18.86) * mm, "end": v(8.38, 18.16) * mm});
            skLineSegment(sketch, "E270", {"start": v(8.38, 18.16) * mm, "end": v(7.93, 17.44) * mm});
            skArc(sketch, "E271", {"start": v(7.55, 17.33) * mm, "mid": v(7.76, 17.31) * mm, "end": v(7.93, 17.44) * mm});
            skLineSegment(sketch, "E272", {"start": v(6.17, 20.07) * mm, "end": v(5.44, 19.25) * mm});
            skLineSegment(sketch, "E273", {"start": v(5.44, 19.25) * mm, "end": v(5.1, 18.46) * mm});
            skArc(sketch, "E274", {"start": v(4.75, 18.3) * mm, "mid": v(4.96, 18.31) * mm, "end": v(5.1, 18.46) * mm});
            skLineSegment(sketch, "E275", {"start": v(2.96, 20.8) * mm, "end": v(2.36, 19.86) * mm});
            skLineSegment(sketch, "E276", {"start": v(2.36, 19.86) * mm, "end": v(2.15, 19.04) * mm});
            skArc(sketch, "E277", {"start": v(1.83, 18.81) * mm, "mid": v(2.03, 18.86) * mm, "end": v(2.15, 19.04) * mm});
            skLineSegment(sketch, "E278", {"start": v(-0.33, 21) * mm, "end": v(-0.78, 19.98) * mm});
            skLineSegment(sketch, "E279", {"start": v(-0.78, 19.98) * mm, "end": v(-0.86, 19.14) * mm});
            skArc(sketch, "E280", {"start": v(-1.14, 18.87) * mm, "mid": v(-0.95, 18.95) * mm, "end": v(-0.86, 19.14) * mm});
            skLineSegment(sketch, "E281", {"start": v(-3.61, 20.69) * mm, "end": v(-3.9, 19.62) * mm});
            skLineSegment(sketch, "E282", {"start": v(-3.9, 19.62) * mm, "end": v(-3.84, 18.77) * mm});
            skArc(sketch, "E283", {"start": v(-4.07, 18.46) * mm, "mid": v(-3.9, 18.57) * mm, "end": v(-3.84, 18.77) * mm});
            skLineSegment(sketch, "E284", {"start": v(-6.8, 19.87) * mm, "end": v(-6.91, 18.77) * mm});
            skLineSegment(sketch, "E285", {"start": v(-6.91, 18.77) * mm, "end": v(-6.73, 17.94) * mm});
            skArc(sketch, "E286", {"start": v(-6.91, 17.6) * mm, "mid": v(-6.76, 17.73) * mm, "end": v(-6.73, 17.94) * mm});
            skLineSegment(sketch, "E287", {"start": v(-9.83, 18.56) * mm, "end": v(-9.76, 17.45) * mm});
            skLineSegment(sketch, "E288", {"start": v(-9.76, 17.45) * mm, "end": v(-9.45, 16.66) * mm});
            skArc(sketch, "E289", {"start": v(-9.58, 16.3) * mm, "mid": v(-9.45, 16.45) * mm, "end": v(-9.45, 16.66) * mm});
            skLineSegment(sketch, "E290", {"start": v(-12.61, 16.8) * mm, "end": v(-12.37, 15.71) * mm});
            skLineSegment(sketch, "E291", {"start": v(-12.37, 15.71) * mm, "end": v(-11.94, 14.98) * mm});
            skArc(sketch, "E292", {"start": v(-12, 14.6) * mm, "mid": v(-11.9, 14.77) * mm, "end": v(-11.94, 14.98) * mm});
            skLineSegment(sketch, "E293", {"start": v(-15.08, 14.61) * mm, "end": v(-14.68, 13.58) * mm});
            skLineSegment(sketch, "E294", {"start": v(-14.68, 13.58) * mm, "end": v(-14.14, 12.93) * mm});
            skArc(sketch, "E295", {"start": v(-14.14, 12.54) * mm, "mid": v(-14.07, 12.73) * mm, "end": v(-14.14, 12.93) * mm});
            skLineSegment(sketch, "E296", {"start": v(-17.18, 12.07) * mm, "end": v(-16.62, 11.12) * mm});
            skLineSegment(sketch, "E297", {"start": v(-16.62, 11.12) * mm, "end": v(-15.98, 10.56) * mm});
            skArc(sketch, "E298", {"start": v(-15.93, 10.17) * mm, "mid": v(-15.89, 10.37) * mm, "end": v(-15.98, 10.56) * mm});
            skLineSegment(sketch, "E299", {"start": v(-18.86, 9.24) * mm, "end": v(-18.16, 8.38) * mm});
            skLineSegment(sketch, "E300", {"start": v(-18.16, 8.38) * mm, "end": v(-17.44, 7.93) * mm});
            skArc(sketch, "E301", {"start": v(-17.33, 7.55) * mm, "mid": v(-17.31, 7.76) * mm, "end": v(-17.44, 7.93) * mm});
            skLineSegment(sketch, "E302", {"start": v(-20.07, 6.17) * mm, "end": v(-19.25, 5.44) * mm});
            skLineSegment(sketch, "E303", {"start": v(-19.25, 5.44) * mm, "end": v(-18.46, 5.1) * mm});
            skArc(sketch, "E304", {"start": v(-18.3, 4.75) * mm, "mid": v(-18.31, 4.96) * mm, "end": v(-18.46, 5.1) * mm});
            skLineSegment(sketch, "E305", {"start": v(-20.8, 2.96) * mm, "end": v(-19.86, 2.36) * mm});
            skLineSegment(sketch, "E306", {"start": v(-19.86, 2.36) * mm, "end": v(-19.04, 2.15) * mm});
            skArc(sketch, "E307", {"start": v(-18.81, 1.83) * mm, "mid": v(-18.86, 2.03) * mm, "end": v(-19.04, 2.15) * mm});
            skArc(sketch, "E308", {"start": v(21, 0) * mm, "mid": v(21, 0.17) * mm, "end": v(21, 0.33) * mm});
            skArc(sketch, "E309", {"start": v(20.8, 2.96) * mm, "mid": v(20.74, 3.29) * mm, "end": v(20.69, 3.61) * mm});
            skArc(sketch, "E310", {"start": v(20.07, 6.17) * mm, "mid": v(19.97, 6.49) * mm, "end": v(19.87, 6.8) * mm});
            skArc(sketch, "E311", {"start": v(18.86, 9.24) * mm, "mid": v(18.71, 9.53) * mm, "end": v(18.56, 9.83) * mm});
            skArc(sketch, "E312", {"start": v(17.18, 12.07) * mm, "mid": v(16.99, 12.34) * mm, "end": v(16.8, 12.61) * mm});
            skArc(sketch, "E313", {"start": v(15.08, 14.61) * mm, "mid": v(14.85, 14.85) * mm, "end": v(14.61, 15.08) * mm});
            skArc(sketch, "E314", {"start": v(12.61, 16.8) * mm, "mid": v(12.34, 16.99) * mm, "end": v(12.07, 17.18) * mm});
            skArc(sketch, "E315", {"start": v(9.83, 18.56) * mm, "mid": v(9.53, 18.71) * mm, "end": v(9.24, 18.86) * mm});
            skArc(sketch, "E316", {"start": v(6.8, 19.87) * mm, "mid": v(6.49, 19.97) * mm, "end": v(6.17, 20.07) * mm});
            skArc(sketch, "E317", {"start": v(3.61, 20.69) * mm, "mid": v(3.29, 20.74) * mm, "end": v(2.96, 20.8) * mm});
            skArc(sketch, "E318", {"start": v(0.33, 21) * mm, "mid": v(0, 21) * mm, "end": v(-0.33, 21) * mm});
            skArc(sketch, "E319", {"start": v(-2.96, 20.8) * mm, "mid": v(-3.29, 20.74) * mm, "end": v(-3.61, 20.69) * mm});
            skArc(sketch, "E320", {"start": v(-6.17, 20.07) * mm, "mid": v(-6.49, 19.97) * mm, "end": v(-6.8, 19.87) * mm});
            skArc(sketch, "E321", {"start": v(-9.24, 18.86) * mm, "mid": v(-9.53, 18.71) * mm, "end": v(-9.83, 18.56) * mm});
            skArc(sketch, "E322", {"start": v(-12.07, 17.18) * mm, "mid": v(-12.34, 16.99) * mm, "end": v(-12.61, 16.8) * mm});
            skArc(sketch, "E323", {"start": v(-14.61, 15.08) * mm, "mid": v(-14.85, 14.85) * mm, "end": v(-15.08, 14.61) * mm});
            skArc(sketch, "E324", {"start": v(-16.8, 12.61) * mm, "mid": v(-16.99, 12.34) * mm, "end": v(-17.18, 12.07) * mm});
            skArc(sketch, "E325", {"start": v(-18.56, 9.83) * mm, "mid": v(-18.71, 9.53) * mm, "end": v(-18.86, 9.24) * mm});
            skArc(sketch, "E326", {"start": v(-19.87, 6.8) * mm, "mid": v(-19.97, 6.49) * mm, "end": v(-20.07, 6.17) * mm});
            skArc(sketch, "E327", {"start": v(-20.69, 3.61) * mm, "mid": v(-20.74, 3.29) * mm, "end": v(-20.8, 2.96) * mm});
            skArc(sketch, "E328", {"start": v(-21, 0.33) * mm, "mid": v(-21, 0.17) * mm, "end": v(-21, 0) * mm});
            skArc(sketch, "E329", {"start": v(-20.8, -2.96) * mm, "mid": v(-20.74, -3.29) * mm, "end": v(-20.69, -3.61) * mm});
            skArc(sketch, "E330", {"start": v(-20.07, -6.17) * mm, "mid": v(-19.97, -6.49) * mm, "end": v(-19.87, -6.8) * mm});
            skArc(sketch, "E331", {"start": v(-18.86, -9.24) * mm, "mid": v(-18.71, -9.53) * mm, "end": v(-18.56, -9.83) * mm});
            skArc(sketch, "E332", {"start": v(-17.18, -12.07) * mm, "mid": v(-16.99, -12.34) * mm, "end": v(-16.8, -12.61) * mm});
            skArc(sketch, "E333", {"start": v(-15.08, -14.61) * mm, "mid": v(-14.85, -14.85) * mm, "end": v(-14.61, -15.08) * mm});
            skArc(sketch, "E334", {"start": v(-12.61, -16.8) * mm, "mid": v(-12.34, -16.99) * mm, "end": v(-12.07, -17.18) * mm});
            skArc(sketch, "E335", {"start": v(-9.83, -18.56) * mm, "mid": v(-9.53, -18.71) * mm, "end": v(-9.24, -18.86) * mm});
            skArc(sketch, "E336", {"start": v(-6.8, -19.87) * mm, "mid": v(-6.49, -19.97) * mm, "end": v(-6.17, -20.07) * mm});
            skArc(sketch, "E337", {"start": v(-3.61, -20.69) * mm, "mid": v(-3.29, -20.74) * mm, "end": v(-2.96, -20.8) * mm});
            skArc(sketch, "E338", {"start": v(-0.33, -21) * mm, "mid": v(0, -21) * mm, "end": v(0.33, -21) * mm});
            skArc(sketch, "E339", {"start": v(2.96, -20.8) * mm, "mid": v(3.29, -20.74) * mm, "end": v(3.61, -20.69) * mm});
            skArc(sketch, "E340", {"start": v(6.17, -20.07) * mm, "mid": v(6.49, -19.97) * mm, "end": v(6.8, -19.87) * mm});
            skArc(sketch, "E341", {"start": v(9.24, -18.86) * mm, "mid": v(9.53, -18.71) * mm, "end": v(9.83, -18.56) * mm});
            skArc(sketch, "E342", {"start": v(12.07, -17.18) * mm, "mid": v(12.34, -16.99) * mm, "end": v(12.61, -16.8) * mm});
            skArc(sketch, "E343", {"start": v(14.61, -15.08) * mm, "mid": v(14.85, -14.85) * mm, "end": v(15.08, -14.61) * mm});
            skArc(sketch, "E344", {"start": v(16.8, -12.61) * mm, "mid": v(16.99, -12.34) * mm, "end": v(17.18, -12.07) * mm});
            skArc(sketch, "E345", {"start": v(18.56, -9.83) * mm, "mid": v(18.71, -9.53) * mm, "end": v(18.86, -9.24) * mm});
            skArc(sketch, "E346", {"start": v(19.87, -6.8) * mm, "mid": v(19.97, -6.49) * mm, "end": v(20.07, -6.17) * mm});
            skArc(sketch, "E347", {"start": v(20.69, -3.61) * mm, "mid": v(20.74, -3.29) * mm, "end": v(20.8, -2.96) * mm});
            skArc(sketch, "E348", {"start": v(0, 5) * mm, "mid": v(-5, 0) * mm, "end": v(0, -5) * mm});
            skArc(sketch, "E349", {"start": v(12.5, 0) * mm, "mid": v(0, 12.5) * mm, "end": v(-12.5, 0) * mm});
            skSolve(sketch);
        }
        {
            var Q0;
            {var subQ3=sQuery(id+"F4.wireOp",EDGE,"E42");Q0=makeQuery(id+"F4.imprint","IMPRINT",FACE,{"disambiguationData":[TD([[makeQuery(id+"F4.imprint","IMPRINT",EDGE,{"derivedFrom":subQ3}),-1.0]])]});}
            var Q1;
            Q1=makeQuery(id+"F4.imprint","IMPRINT",FACE,{"disambiguationData":[TD([[makeQuery(id+"F4.imprint","IMPRINT",EDGE,{"derivedFrom":sQuery(id+"F4.wireOp",EDGE,"E52")}),-1.0]])]});
            var Q2;
            Q2=makeQuery(id+"F4.imprint","IMPRINT",FACE,{"disambiguationData":[TD([[makeQuery(id+"F4.imprint","IMPRINT",EDGE,{"derivedFrom":sQuery(id+"F4.wireOp",EDGE,"E121")}),-1.0]])]});
            var Q3;
            {var subQ6=sQuery(id+"F4.wireOp",EDGE,"E113");Q3=makeQuery(id+"F4.imprint","IMPRINT",FACE,{"disambiguationData":[TD([[makeQuery(id+"F4.imprint","IMPRINT",EDGE,{"derivedFrom":subQ6}),-1.0]])]});}
            var Q4;
            Q4=makeQuery(id+"F4.imprint","IMPRINT",FACE,{"disambiguationData":[TD([[makeQuery(id+"F4.imprint","IMPRINT",EDGE,{"derivedFrom":sQuery(id+"F4.wireOp",EDGE,"E24")}),1.0]])]});
            var Q5;
            Q5=makeQuery(id+"F4.imprint","IMPRINT",FACE,{"disambiguationData":[TD([[makeQuery(id+"F4.imprint","IMPRINT",EDGE,{"derivedFrom":sQuery(id+"F4.wireOp",EDGE,"E25")}),1.0]])]});
            extrude(context, id + "F5", {"entities" : qUnion([Q0, Q1, Q2, Q3, Q4, Q5]), "operationType" : NewBodyOperationType.ADD, "depth" : 9 * mm});
        }
        {
            var Q0;
            Q0=makeQuery(id+"F5.opExtrude","CAP_FACE",FACE,{"disambiguationData":[OSD([sQuery(id+"F4.wireOp",EDGE,"E24"),sQuery(id+"F4.wireOp",EDGE,"E26"),sQuery(id+"F4.wireOp",EDGE,"E27"),sQuery(id+"F4.wireOp",EDGE,"E28"),sQuery(id+"F4.wireOp",EDGE,"E29"),sQuery(id+"F4.wireOp",EDGE,"E30"),sQuery(id+"F4.wireOp",EDGE,"E31"),sQuery(id+"F4.wireOp",EDGE,"E32"),sQuery(id+"F4.wireOp",EDGE,"E33"),sQuery(id+"F4.wireOp",EDGE,"E34"),sQuery(id+"F4.wireOp",EDGE,"E35"),sQuery(id+"F4.wireOp",EDGE,"E36"),sQuery(id+"F4.wireOp",EDGE,"E37"),sQuery(id+"F4.wireOp",EDGE,"E38"),sQuery(id+"F4.wireOp",EDGE,"E39"),sQuery(id+"F4.wireOp",EDGE,"E40"),sQuery(id+"F4.wireOp",EDGE,"E41"),sQuery(id+"F4.wireOp",EDGE,"E42"),sQuery(id+"F4.wireOp",EDGE,"E43"),sQuery(id+"F4.wireOp",EDGE,"E44"),sQuery(id+"F4.wireOp",EDGE,"E45"),sQuery(id+"F4.wireOp",EDGE,"E46"),sQuery(id+"F4.wireOp",EDGE,"E47"),sQuery(id+"F4.wireOp",EDGE,"E48"),sQuery(id+"F4.wireOp",EDGE,"E49"),sQuery(id+"F4.wireOp",EDGE,"E50"),sQuery(id+"F4.wireOp",EDGE,"E51"),sQuery(id+"F4.wireOp",EDGE,"E52"),sQuery(id+"F4.wireOp",EDGE,"E53"),sQuery(id+"F4.wireOp",EDGE,"E54"),sQuery(id+"F4.wireOp",EDGE,"E55"),sQuery(id+"F4.wireOp",EDGE,"E56"),sQuery(id+"F4.wireOp",EDGE,"E57"),sQuery(id+"F4.wireOp",EDGE,"E58"),sQuery(id+"F4.wireOp",EDGE,"E59"),sQuery(id+"F4.wireOp",EDGE,"E60"),sQuery(id+"F4.wireOp",EDGE,"E61"),sQuery(id+"F4.wireOp",EDGE,"E62"),sQuery(id+"F4.wireOp",EDGE,"E63"),sQuery(id+"F4.wireOp",EDGE,"E64"),sQuery(id+"F4.wireOp",EDGE,"E65"),sQuery(id+"F4.wireOp",EDGE,"E66"),sQuery(id+"F4.wireOp",EDGE,"E67"),sQuery(id+"F4.wireOp",EDGE,"E68"),sQuery(id+"F4.wireOp",EDGE,"E69"),sQuery(id+"F4.wireOp",EDGE,"E70"),sQuery(id+"F4.wireOp",EDGE,"E71"),sQuery(id+"F4.wireOp",EDGE,"E72"),sQuery(id+"F4.wireOp",EDGE,"E73"),sQuery(id+"F4.wireOp",EDGE,"E74"),sQuery(id+"F4.wireOp",EDGE,"E75"),sQuery(id+"F4.wireOp",EDGE,"E76"),sQuery(id+"F4.wireOp",EDGE,"E77"),sQuery(id+"F4.wireOp",EDGE,"E78"),sQuery(id+"F4.wireOp",EDGE,"E79"),sQuery(id+"F4.wireOp",EDGE,"E80"),sQuery(id+"F4.wireOp",EDGE,"E81"),sQuery(id+"F4.wireOp",EDGE,"E82"),sQuery(id+"F4.wireOp",EDGE,"E83"),sQuery(id+"F4.wireOp",EDGE,"E84"),sQuery(id+"F4.wireOp",EDGE,"E85"),sQuery(id+"F4.wireOp",EDGE,"E86"),sQuery(id+"F4.wireOp",EDGE,"E87"),sQuery(id+"F4.wireOp",EDGE,"E88"),sQuery(id+"F4.wireOp",EDGE,"E89"),sQuery(id+"F4.wireOp",EDGE,"E90"),sQuery(id+"F4.wireOp",EDGE,"E91"),sQuery(id+"F4.wireOp",EDGE,"E92"),sQuery(id+"F4.wireOp",EDGE,"E93"),sQuery(id+"F4.wireOp",EDGE,"E94"),sQuery(id+"F4.wireOp",EDGE,"E95"),sQuery(id+"F4.wireOp",EDGE,"E96"),sQuery(id+"F4.wireOp",EDGE,"E97"),sQuery(id+"F4.wireOp",EDGE,"E98"),sQuery(id+"F4.wireOp",EDGE,"E99"),sQuery(id+"F4.wireOp",EDGE,"E100"),sQuery(id+"F4.wireOp",EDGE,"E101"),sQuery(id+"F4.wireOp",EDGE,"E102"),sQuery(id+"F4.wireOp",EDGE,"E103"),sQuery(id+"F4.wireOp",EDGE,"E104"),sQuery(id+"F4.wireOp",EDGE,"E105"),sQuery(id+"F4.wireOp",EDGE,"E106"),sQuery(id+"F4.wireOp",EDGE,"E107"),sQuery(id+"F4.wireOp",EDGE,"E108"),sQuery(id+"F4.wireOp",EDGE,"E109"),sQuery(id+"F4.wireOp",EDGE,"E110"),sQuery(id+"F4.wireOp",EDGE,"E111"),sQuery(id+"F4.wireOp",EDGE,"E112"),sQuery(id+"F4.wireOp",EDGE,"E113"),sQuery(id+"F4.wireOp",EDGE,"E114"),sQuery(id+"F4.wireOp",EDGE,"E115"),sQuery(id+"F4.wireOp",EDGE,"E116"),sQuery(id+"F4.wireOp",EDGE,"E117"),sQuery(id+"F4.wireOp",EDGE,"E118"),sQuery(id+"F4.wireOp",EDGE,"E119"),sQuery(id+"F4.wireOp",EDGE,"E120"),sQuery(id+"F4.wireOp",EDGE,"E121"),sQuery(id+"F4.wireOp",EDGE,"E122"),sQuery(id+"F4.wireOp",EDGE,"E123"),sQuery(id+"F4.wireOp",EDGE,"E124"),sQuery(id+"F4.wireOp",EDGE,"E125"),sQuery(id+"F4.wireOp",EDGE,"E126"),sQuery(id+"F4.wireOp",EDGE,"E127"),sQuery(id+"F4.wireOp",EDGE,"E128"),sQuery(id+"F4.wireOp",EDGE,"E129"),sQuery(id+"F4.wireOp",EDGE,"E130"),sQuery(id+"F4.wireOp",EDGE,"E131"),sQuery(id+"F4.wireOp",EDGE,"E132"),sQuery(id+"F4.wireOp",EDGE,"E133"),sQuery(id+"F4.wireOp",EDGE,"E134"),sQuery(id+"F4.wireOp",EDGE,"E135"),sQuery(id+"F4.wireOp",EDGE,"E136"),sQuery(id+"F4.wireOp",EDGE,"E137"),sQuery(id+"F4.wireOp",EDGE,"E138"),sQuery(id+"F4.wireOp",EDGE,"E139"),sQuery(id+"F4.wireOp",EDGE,"E140"),sQuery(id+"F4.wireOp",EDGE,"E141"),sQuery(id+"F4.wireOp",EDGE,"E142"),sQuery(id+"F4.wireOp",EDGE,"E143"),sQuery(id+"F4.wireOp",EDGE,"E144"),sQuery(id+"F4.wireOp",EDGE,"E145"),sQuery(id+"F4.wireOp",EDGE,"E146"),sQuery(id+"F4.wireOp",EDGE,"E147"),sQuery(id+"F4.wireOp",EDGE,"E148"),sQuery(id+"F4.wireOp",EDGE,"E149"),sQuery(id+"F4.wireOp",EDGE,"E150"),sQuery(id+"F4.wireOp",EDGE,"E151"),sQuery(id+"F4.wireOp",EDGE,"E152"),sQuery(id+"F4.wireOp",EDGE,"E153"),sQuery(id+"F4.wireOp",EDGE,"E154"),sQuery(id+"F4.wireOp",EDGE,"E155"),sQuery(id+"F4.wireOp",EDGE,"E156"),sQuery(id+"F4.wireOp",EDGE,"E157"),sQuery(id+"F4.wireOp",EDGE,"E158"),sQuery(id+"F4.wireOp",EDGE,"E159"),sQuery(id+"F4.wireOp",EDGE,"E160"),sQuery(id+"F4.wireOp",EDGE,"E161"),sQuery(id+"F4.wireOp",EDGE,"E162"),sQuery(id+"F4.wireOp",EDGE,"E163"),sQuery(id+"F4.wireOp",EDGE,"E164"),sQuery(id+"F4.wireOp",EDGE,"E165"),sQuery(id+"F4.wireOp",EDGE,"E166"),sQuery(id+"F4.wireOp",EDGE,"E167"),sQuery(id+"F4.wireOp",EDGE,"E168"),sQuery(id+"F4.wireOp",EDGE,"E169"),sQuery(id+"F4.wireOp",EDGE,"E170"),sQuery(id+"F4.wireOp",EDGE,"E171"),sQuery(id+"F4.wireOp",EDGE,"E172"),sQuery(id+"F4.wireOp",EDGE,"E173"),sQuery(id+"F4.wireOp",EDGE,"E174"),sQuery(id+"F4.wireOp",EDGE,"E175"),sQuery(id+"F4.wireOp",EDGE,"E176"),sQuery(id+"F4.wireOp",EDGE,"E177"),sQuery(id+"F4.wireOp",EDGE,"E178"),sQuery(id+"F4.wireOp",EDGE,"E179"),sQuery(id+"F4.wireOp",EDGE,"E180"),sQuery(id+"F4.wireOp",EDGE,"E181"),sQuery(id+"F4.wireOp",EDGE,"E182"),sQuery(id+"F4.wireOp",EDGE,"E183"),sQuery(id+"F4.wireOp",EDGE,"E184"),sQuery(id+"F4.wireOp",EDGE,"E185"),sQuery(id+"F4.wireOp",EDGE,"E186"),sQuery(id+"F4.wireOp",EDGE,"E187"),sQuery(id+"F4.wireOp",EDGE,"E188"),sQuery(id+"F4.wireOp",EDGE,"E189"),sQuery(id+"F4.wireOp",EDGE,"E190"),sQuery(id+"F4.wireOp",EDGE,"E191"),sQuery(id+"F4.wireOp",EDGE,"E192"),sQuery(id+"F4.wireOp",EDGE,"E193"),sQuery(id+"F4.wireOp",EDGE,"E194"),sQuery(id+"F4.wireOp",EDGE,"E195"),sQuery(id+"F4.wireOp",EDGE,"E196"),sQuery(id+"F4.wireOp",EDGE,"E197"),sQuery(id+"F4.wireOp",EDGE,"E198"),sQuery(id+"F4.wireOp",EDGE,"E199"),sQuery(id+"F4.wireOp",EDGE,"E200"),sQuery(id+"F4.wireOp",EDGE,"E201"),sQuery(id+"F4.wireOp",EDGE,"E202"),sQuery(id+"F4.wireOp",EDGE,"E203"),sQuery(id+"F4.wireOp",EDGE,"E204"),sQuery(id+"F4.wireOp",EDGE,"E205"),sQuery(id+"F4.wireOp",EDGE,"E206"),sQuery(id+"F4.wireOp",EDGE,"E207"),sQuery(id+"F4.wireOp",EDGE,"E208"),sQuery(id+"F4.wireOp",EDGE,"E209"),sQuery(id+"F4.wireOp",EDGE,"E210"),sQuery(id+"F4.wireOp",EDGE,"E211"),sQuery(id+"F4.wireOp",EDGE,"E212"),sQuery(id+"F4.wireOp",EDGE,"E213"),sQuery(id+"F4.wireOp",EDGE,"E214"),sQuery(id+"F4.wireOp",EDGE,"E215"),sQuery(id+"F4.wireOp",EDGE,"E216"),sQuery(id+"F4.wireOp",EDGE,"E217"),sQuery(id+"F4.wireOp",EDGE,"E218"),sQuery(id+"F4.wireOp",EDGE,"E219"),sQuery(id+"F4.wireOp",EDGE,"E220"),sQuery(id+"F4.wireOp",EDGE,"E221"),sQuery(id+"F4.wireOp",EDGE,"E222"),sQuery(id+"F4.wireOp",EDGE,"E223"),sQuery(id+"F4.wireOp",EDGE,"E224"),sQuery(id+"F4.wireOp",EDGE,"E225"),sQuery(id+"F4.wireOp",EDGE,"E226"),sQuery(id+"F4.wireOp",EDGE,"E227"),sQuery(id+"F4.wireOp",EDGE,"E228"),sQuery(id+"F4.wireOp",EDGE,"E229"),sQuery(id+"F4.wireOp",EDGE,"E230"),sQuery(id+"F4.wireOp",EDGE,"E231"),sQuery(id+"F4.wireOp",EDGE,"E232"),sQuery(id+"F4.wireOp",EDGE,"E233"),sQuery(id+"F4.wireOp",EDGE,"E234"),sQuery(id+"F4.wireOp",EDGE,"E235"),sQuery(id+"F4.wireOp",EDGE,"E236"),sQuery(id+"F4.wireOp",EDGE,"E237"),sQuery(id+"F4.wireOp",EDGE,"E238"),sQuery(id+"F4.wireOp",EDGE,"E239"),sQuery(id+"F4.wireOp",EDGE,"E240"),sQuery(id+"F4.wireOp",EDGE,"E241"),sQuery(id+"F4.wireOp",EDGE,"E242"),sQuery(id+"F4.wireOp",EDGE,"E243"),sQuery(id+"F4.wireOp",EDGE,"E244"),sQuery(id+"F4.wireOp",EDGE,"E245"),sQuery(id+"F4.wireOp",EDGE,"E246"),sQuery(id+"F4.wireOp",EDGE,"E247"),sQuery(id+"F4.wireOp",EDGE,"E248"),sQuery(id+"F4.wireOp",EDGE,"E249"),sQuery(id+"F4.wireOp",EDGE,"E250"),sQuery(id+"F4.wireOp",EDGE,"E251"),sQuery(id+"F4.wireOp",EDGE,"E252"),sQuery(id+"F4.wireOp",EDGE,"E253"),sQuery(id+"F4.wireOp",EDGE,"E254"),sQuery(id+"F4.wireOp",EDGE,"E255"),sQuery(id+"F4.wireOp",EDGE,"E256"),sQuery(id+"F4.wireOp",EDGE,"E257"),sQuery(id+"F4.wireOp",EDGE,"E258"),sQuery(id+"F4.wireOp",EDGE,"E259"),sQuery(id+"F4.wireOp",EDGE,"E260"),sQuery(id+"F4.wireOp",EDGE,"E261"),sQuery(id+"F4.wireOp",EDGE,"E262"),sQuery(id+"F4.wireOp",EDGE,"E263"),sQuery(id+"F4.wireOp",EDGE,"E264"),sQuery(id+"F4.wireOp",EDGE,"E265"),sQuery(id+"F4.wireOp",EDGE,"E266"),sQuery(id+"F4.wireOp",EDGE,"E267"),sQuery(id+"F4.wireOp",EDGE,"E268"),sQuery(id+"F4.wireOp",EDGE,"E269"),sQuery(id+"F4.wireOp",EDGE,"E270"),sQuery(id+"F4.wireOp",EDGE,"E271"),sQuery(id+"F4.wireOp",EDGE,"E272"),sQuery(id+"F4.wireOp",EDGE,"E273"),sQuery(id+"F4.wireOp",EDGE,"E274"),sQuery(id+"F4.wireOp",EDGE,"E275"),sQuery(id+"F4.wireOp",EDGE,"E276"),sQuery(id+"F4.wireOp",EDGE,"E277"),sQuery(id+"F4.wireOp",EDGE,"E278"),sQuery(id+"F4.wireOp",EDGE,"E279"),sQuery(id+"F4.wireOp",EDGE,"E280"),sQuery(id+"F4.wireOp",EDGE,"E281"),sQuery(id+"F4.wireOp",EDGE,"E282"),sQuery(id+"F4.wireOp",EDGE,"E283"),sQuery(id+"F4.wireOp",EDGE,"E284"),sQuery(id+"F4.wireOp",EDGE,"E285"),sQuery(id+"F4.wireOp",EDGE,"E286"),sQuery(id+"F4.wireOp",EDGE,"E287"),sQuery(id+"F4.wireOp",EDGE,"E288"),sQuery(id+"F4.wireOp",EDGE,"E289"),sQuery(id+"F4.wireOp",EDGE,"E290"),sQuery(id+"F4.wireOp",EDGE,"E291"),sQuery(id+"F4.wireOp",EDGE,"E292"),sQuery(id+"F4.wireOp",EDGE,"E293"),sQuery(id+"F4.wireOp",EDGE,"E294"),sQuery(id+"F4.wireOp",EDGE,"E295"),sQuery(id+"F4.wireOp",EDGE,"E296"),sQuery(id+"F4.wireOp",EDGE,"E297"),sQuery(id+"F4.wireOp",EDGE,"E298"),sQuery(id+"F4.wireOp",EDGE,"E299"),sQuery(id+"F4.wireOp",EDGE,"E300"),sQuery(id+"F4.wireOp",EDGE,"E301"),sQuery(id+"F4.wireOp",EDGE,"E302"),sQuery(id+"F4.wireOp",EDGE,"E303"),sQuery(id+"F4.wireOp",EDGE,"E304"),sQuery(id+"F4.wireOp",EDGE,"E305"),sQuery(id+"F4.wireOp",EDGE,"E306"),sQuery(id+"F4.wireOp",EDGE,"E307"),sQuery(id+"F4.wireOp",EDGE,"E308"),sQuery(id+"F4.wireOp",EDGE,"E309"),sQuery(id+"F4.wireOp",EDGE,"E310"),sQuery(id+"F4.wireOp",EDGE,"E311"),sQuery(id+"F4.wireOp",EDGE,"E312"),sQuery(id+"F4.wireOp",EDGE,"E313"),sQuery(id+"F4.wireOp",EDGE,"E314"),sQuery(id+"F4.wireOp",EDGE,"E315"),sQuery(id+"F4.wireOp",EDGE,"E316"),sQuery(id+"F4.wireOp",EDGE,"E317"),sQuery(id+"F4.wireOp",EDGE,"E318"),sQuery(id+"F4.wireOp",EDGE,"E319"),sQuery(id+"F4.wireOp",EDGE,"E320"),sQuery(id+"F4.wireOp",EDGE,"E321"),sQuery(id+"F4.wireOp",EDGE,"E322"),sQuery(id+"F4.wireOp",EDGE,"E323"),sQuery(id+"F4.wireOp",EDGE,"E324"),sQuery(id+"F4.wireOp",EDGE,"E325"),sQuery(id+"F4.wireOp",EDGE,"E326"),sQuery(id+"F4.wireOp",EDGE,"E327"),sQuery(id+"F4.wireOp",EDGE,"E328"),sQuery(id+"F4.wireOp",EDGE,"E329"),sQuery(id+"F4.wireOp",EDGE,"E330"),sQuery(id+"F4.wireOp",EDGE,"E331"),sQuery(id+"F4.wireOp",EDGE,"E332"),sQuery(id+"F4.wireOp",EDGE,"E333"),sQuery(id+"F4.wireOp",EDGE,"E334"),sQuery(id+"F4.wireOp",EDGE,"E335"),sQuery(id+"F4.wireOp",EDGE,"E336"),sQuery(id+"F4.wireOp",EDGE,"E337"),sQuery(id+"F4.wireOp",EDGE,"E338"),sQuery(id+"F4.wireOp",EDGE,"E339"),sQuery(id+"F4.wireOp",EDGE,"E340"),sQuery(id+"F4.wireOp",EDGE,"E341"),sQuery(id+"F4.wireOp",EDGE,"E342"),sQuery(id+"F4.wireOp",EDGE,"E343"),sQuery(id+"F4.wireOp",EDGE,"E344"),sQuery(id+"F4.wireOp",EDGE,"E345"),sQuery(id+"F4.wireOp",EDGE,"E346"),sQuery(id+"F4.wireOp",EDGE,"E347"),sQuery(id+"F4.wireOp",EDGE,"E348")])],"isStart":false});
            var sketch = newSketch(context, id + "F6", { "sketchPlane" : qUnion([Q0])});
            skCircle(sketch, "E350", {"center": v(0, 0) * mm, "radius": 9.05 * mm});
            skSolve(sketch);
        }
        {
            var Q0;
            Q0=makeQuery(id+"F6.imprint","IMPRINT",FACE,{"disambiguationData":[TD([[makeQuery(id+"F6.imprint","IMPRINT",EDGE,{"derivedFrom":sQuery(id+"F6.wireOp",EDGE,"E350")}),1.0]])]});
            extrude(context, id + "F7", {"entities" : qUnion([Q0]), "operationType" : NewBodyOperationType.REMOVE, "endBound" : BoundingType.THROUGH_ALL, "oppositeDirection" : true, "depth" : 25 * mm});
        }
    });
